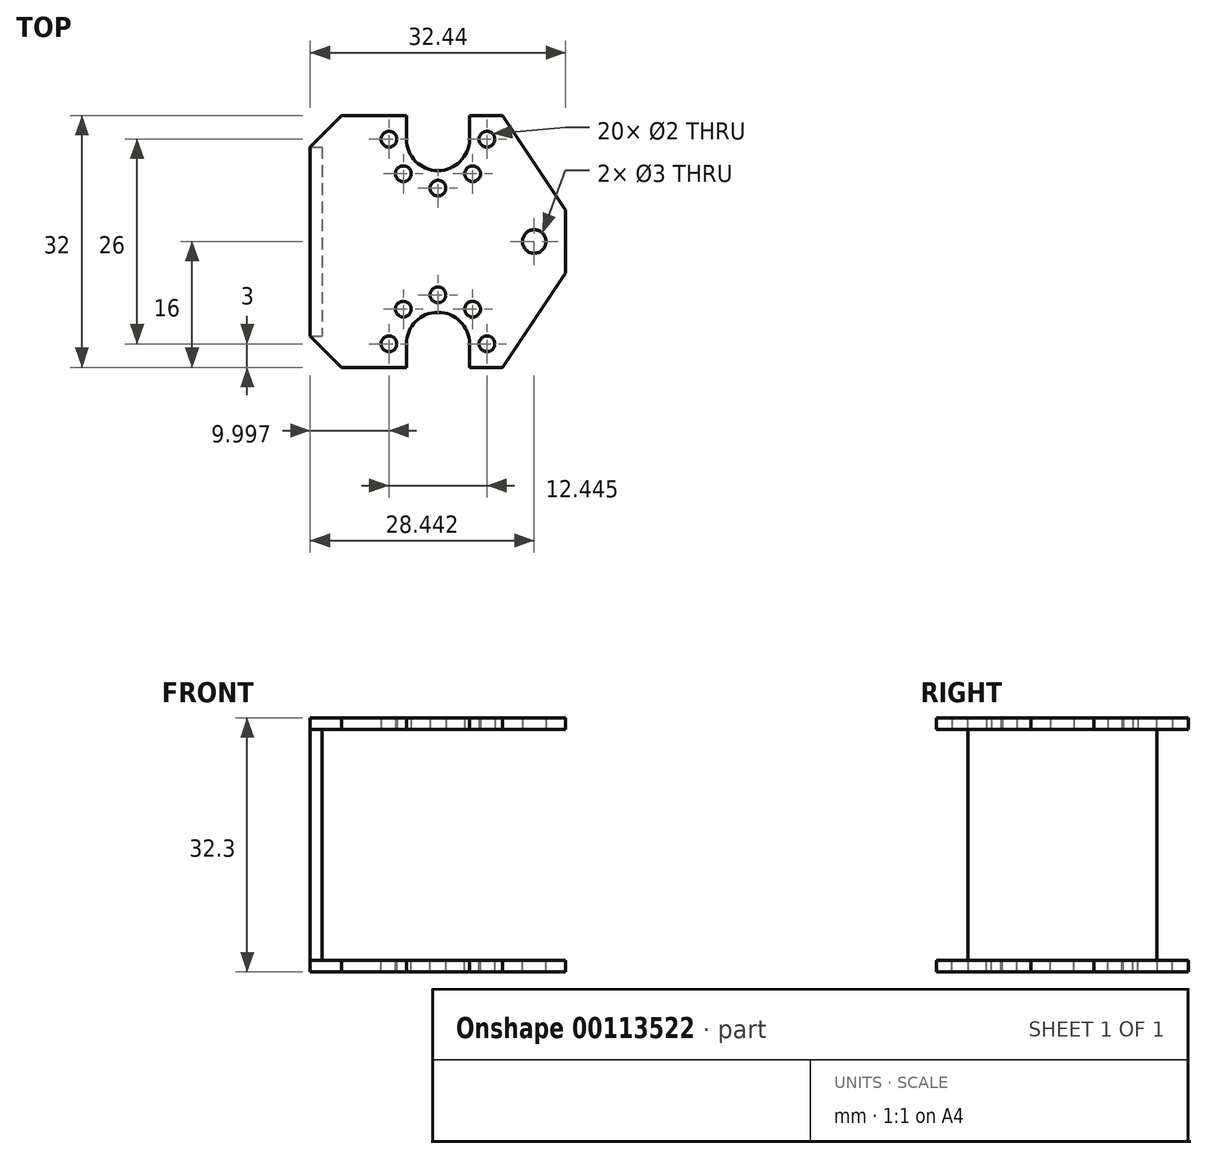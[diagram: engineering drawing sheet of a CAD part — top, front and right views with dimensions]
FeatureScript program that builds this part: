
annotation { "Feature Type Name" : "Feature", "Feature Type Description" : "" }
export const myFeature = defineFeature(function(context is Context, id is Id, definition is map)
    precondition{}
    {
        {
            var Q0;
            Q0=qCreatedBy(makeId("Top.planeOp"),FACE);
            var sketch = newSketch(context, id + "F0", { "sketchPlane" : qUnion([Q0])});
            skLineSegment(sketch, "E0.bottom", {"start": v(-16.22, 16) * mm, "end": v(-4, 16) * mm});
            skLineSegment(sketch, "E0.top", {"start": v(-16.22, -16) * mm, "end": v(-4, -16) * mm});
            skLineSegment(sketch, "E0.left", {"start": v(-16.22, 16) * mm, "end": v(-16.22, -16) * mm});
            skLineSegment(sketch, "E0.right", {"start": v(16.22, 16) * mm, "end": v(16.22, -16) * mm});
            skPoint(sketch, "E0.middle", {"position": v(0, 0) * mm});
            skArc(sketch, "E1", {"start": v(-4, 13) * mm, "mid": v(0, 9) * mm, "end": v(4, 13) * mm});
            skLineSegment(sketch, "E2.bottom", {"start": v(4.4, 8.6) * mm, "end": v(-4.4, 8.6) * mm, "construction": true});
            skLineSegment(sketch, "E2.top", {"start": v(4.4, 17.4) * mm, "end": v(-4.4, 17.4) * mm, "construction": true});
            skLineSegment(sketch, "E2.left", {"start": v(4.4, 8.6) * mm, "end": v(4.4, 17.4) * mm, "construction": true});
            skLineSegment(sketch, "E2.right", {"start": v(-4.4, 8.6) * mm, "end": v(-4.4, 17.4) * mm, "construction": true});
            skCircle(sketch, "E3", {"center": v(4.4, 8.6) * mm, "radius": 1 * mm});
            skCircle(sketch, "E4.1.0", {"center": v(6.22, 13) * mm, "radius": 1 * mm});
            skCircle(sketch, "E4.5.0", {"center": v(-6.22, 13) * mm, "radius": 1 * mm});
            skCircle(sketch, "E4.6.0", {"center": v(-4.4, 8.6) * mm, "radius": 1 * mm});
            skCircle(sketch, "E4.7.0", {"center": v(0, 6.78) * mm, "radius": 1 * mm});
            skLineSegment(sketch, "E5", {"start": v(-4, 13) * mm, "end": v(-4, 16) * mm});
            skLineSegment(sketch, "E6", {"start": v(4, 13) * mm, "end": v(4, 16) * mm});
            skLineSegment(sketch, "E7.trimOffspring", {"start": v(4, 16) * mm, "end": v(16.22, 16) * mm});
            skPoint(sketch, "E8.MirrorP", {"position": v(0, -13) * mm});
            skLineSegment(sketch, "E9.MirrorCS", {"start": v(-4, -13) * mm, "end": v(-4, -16) * mm});
            skCircle(sketch, "E10.MirrorC", {"center": v(0, -6.78) * mm, "radius": 1 * mm});
            skLineSegment(sketch, "E11.MirrorCS", {"start": v(4, -13) * mm, "end": v(4, -16) * mm});
            skCircle(sketch, "E12.MirrorC", {"center": v(-4.4, -8.6) * mm, "radius": 1 * mm});
            skCircle(sketch, "E13.MirrorC", {"center": v(6.22, -13) * mm, "radius": 1 * mm});
            skCircle(sketch, "E14.MirrorC", {"center": v(-6.22, -13) * mm, "radius": 1 * mm});
            skArc(sketch, "E15.MirrorCS", {"start": v(-4, -13) * mm, "mid": v(0, -9) * mm, "end": v(4, -13) * mm});
            skCircle(sketch, "E16.MirrorC", {"center": v(4.4, -8.6) * mm, "radius": 1 * mm});
            skLineSegment(sketch, "E17.trimOffspring", {"start": v(4, -16) * mm, "end": v(16.22, -16) * mm});
            skCircle(sketch, "E18", {"center": v(12.22, 0) * mm, "radius": 1.5 * mm});
            skSolve(sketch);
        }
        {
            var Q0;
            Q0=qSketchRegion(id+"F0",true);
            extrude(context, id + "F1", {"entities" : qUnion([Q0]), "depth" : 1.5 * mm});
        }
        {
            var Q0;
            Q0=makeQuery(id+"F1.opExtrude","CAP_FACE",FACE,{"disambiguationData":[OSD([sQuery(id+"F0.wireOp",EDGE,"E0.bottom"),sQuery(id+"F0.wireOp",EDGE,"E0.top"),sQuery(id+"F0.wireOp",EDGE,"E0.left"),sQuery(id+"F0.wireOp",EDGE,"E0.right"),sQuery(id+"F0.wireOp",EDGE,"E1"),sQuery(id+"F0.wireOp",EDGE,"E3"),sQuery(id+"F0.wireOp",EDGE,"E4.1.0"),sQuery(id+"F0.wireOp",EDGE,"E4.5.0"),sQuery(id+"F0.wireOp",EDGE,"E4.6.0"),sQuery(id+"F0.wireOp",EDGE,"E4.7.0"),sQuery(id+"F0.wireOp",EDGE,"E5"),sQuery(id+"F0.wireOp",EDGE,"E6"),sQuery(id+"F0.wireOp",EDGE,"E7.trimOffspring"),sQuery(id+"F0.wireOp",EDGE,"E9.MirrorCS"),sQuery(id+"F0.wireOp",EDGE,"E10.MirrorC"),sQuery(id+"F0.wireOp",EDGE,"E11.MirrorCS"),sQuery(id+"F0.wireOp",EDGE,"E12.MirrorC"),sQuery(id+"F0.wireOp",EDGE,"E13.MirrorC"),sQuery(id+"F0.wireOp",EDGE,"E14.MirrorC"),sQuery(id+"F0.wireOp",EDGE,"E15.MirrorCS"),sQuery(id+"F0.wireOp",EDGE,"E16.MirrorC"),sQuery(id+"F0.wireOp",EDGE,"E17.trimOffspring")])],"isStart":false});
            var sketch = newSketch(context, id + "F2", { "sketchPlane" : qUnion([Q0])});
            skPoint(sketch, "E19", {"position": v(6.22, 13) * mm});
            skPoint(sketch, "E20", {"position": v(6.22, -13) * mm});
            skLineSegment(sketch, "E21", {"start": v(8.22, 16) * mm, "end": v(16.22, 4) * mm});
            skLineSegment(sketch, "E22", {"start": v(16.22, 4) * mm, "end": v(16.22, 16) * mm});
            skLineSegment(sketch, "E23", {"start": v(16.22, 16) * mm, "end": v(8.22, 16) * mm});
            skLineSegment(sketch, "E24.MirrorCS", {"start": v(16.22, -16) * mm, "end": v(8.22, -16) * mm});
            skLineSegment(sketch, "E25.MirrorCS", {"start": v(16.22, -4) * mm, "end": v(16.22, -16) * mm});
            skLineSegment(sketch, "E26.MirrorCS", {"start": v(8.22, -16) * mm, "end": v(16.22, -4) * mm});
            skLineSegment(sketch, "E27", {"start": v(-16.22, 16) * mm, "end": v(-16.22, 12) * mm});
            skLineSegment(sketch, "E28", {"start": v(-16.22, 12) * mm, "end": v(-12.22, 16) * mm});
            skLineSegment(sketch, "E29", {"start": v(-12.22, 16) * mm, "end": v(-16.22, 16) * mm});
            skLineSegment(sketch, "E30.MirrorCS", {"start": v(-12.22, -16) * mm, "end": v(-16.22, -16) * mm});
            skLineSegment(sketch, "E31.MirrorCS", {"start": v(-16.22, -12) * mm, "end": v(-12.22, -16) * mm});
            skLineSegment(sketch, "E32.MirrorCS", {"start": v(-16.22, -16) * mm, "end": v(-16.22, -12) * mm});
            skSolve(sketch);
        }
        {
            var Q0;
            Q0=qSketchRegion(id+"F2",true);
            extrude(context, id + "F3", {"entities" : qUnion([Q0]), "operationType" : NewBodyOperationType.REMOVE, "endBound" : BoundingType.UP_TO_NEXT, "oppositeDirection" : true, "depth" : 25 * mm});
        }
        {
            var Q0;
            Q0=makeQuery(id+"F1.opExtrude","CAP_FACE",FACE,{"disambiguationData":[OSD([sQuery(id+"F0.wireOp",EDGE,"E0.bottom"),sQuery(id+"F0.wireOp",EDGE,"E0.top"),sQuery(id+"F0.wireOp",EDGE,"E0.left"),sQuery(id+"F0.wireOp",EDGE,"E0.right"),sQuery(id+"F0.wireOp",EDGE,"E1"),sQuery(id+"F0.wireOp",EDGE,"E3"),sQuery(id+"F0.wireOp",EDGE,"E4.1.0"),sQuery(id+"F0.wireOp",EDGE,"E4.5.0"),sQuery(id+"F0.wireOp",EDGE,"E4.6.0"),sQuery(id+"F0.wireOp",EDGE,"E4.7.0"),sQuery(id+"F0.wireOp",EDGE,"E5"),sQuery(id+"F0.wireOp",EDGE,"E6"),sQuery(id+"F0.wireOp",EDGE,"E7.trimOffspring"),sQuery(id+"F0.wireOp",EDGE,"E9.MirrorCS"),sQuery(id+"F0.wireOp",EDGE,"E10.MirrorC"),sQuery(id+"F0.wireOp",EDGE,"E11.MirrorCS"),sQuery(id+"F0.wireOp",EDGE,"E12.MirrorC"),sQuery(id+"F0.wireOp",EDGE,"E13.MirrorC"),sQuery(id+"F0.wireOp",EDGE,"E14.MirrorC"),sQuery(id+"F0.wireOp",EDGE,"E15.MirrorCS"),sQuery(id+"F0.wireOp",EDGE,"E16.MirrorC"),sQuery(id+"F0.wireOp",EDGE,"E17.trimOffspring")])],"isStart":true});
            var sketch = newSketch(context, id + "F4", { "sketchPlane" : qUnion([Q0])});
            skLineSegment(sketch, "E33.bottom", {"start": v(-16.22, -12) * mm, "end": v(-14.72, -12) * mm});
            skLineSegment(sketch, "E33.top", {"start": v(-16.22, 12) * mm, "end": v(-14.72, 12) * mm});
            skLineSegment(sketch, "E33.left", {"start": v(-16.22, -12) * mm, "end": v(-16.22, 12) * mm});
            skLineSegment(sketch, "E33.right", {"start": v(-14.72, -12) * mm, "end": v(-14.72, 12) * mm});
            skSolve(sketch);
        }
        {
            var Q0;
            Q0=qSketchRegion(id+"F4",true);
            extrude(context, id + "F5", {"entities" : qUnion([Q0]), "operationType" : NewBodyOperationType.ADD, "depth" : (29.3 / 2) * mm});
        }
        {
            var Q0;
            Q0=qCreatedBy(makeId("Top.planeOp"),FACE);
            cPlane(context, id + "F6", {"entities" : qUnion([Q0]), "cplaneType" : CPlaneType.OFFSET, "offset" : (29.3 / 2) * mm, "oppositeDirection" : true, "width" : 150 * mm, "height" : 150 * mm});
        }
        {
            var Q0;
            Q0=makeQuery(id+"F1.opExtrude","SWEPT_BODY",BODY,{"disambiguationData":[OSD([sQuery(id+"F0.wireOp",EDGE,"E0.bottom"),sQuery(id+"F0.wireOp",EDGE,"E0.top"),sQuery(id+"F0.wireOp",EDGE,"E0.left"),sQuery(id+"F0.wireOp",EDGE,"E0.right"),sQuery(id+"F0.wireOp",EDGE,"E1"),sQuery(id+"F0.wireOp",EDGE,"E3"),sQuery(id+"F0.wireOp",EDGE,"E4.1.0"),sQuery(id+"F0.wireOp",EDGE,"E4.5.0"),sQuery(id+"F0.wireOp",EDGE,"E4.6.0"),sQuery(id+"F0.wireOp",EDGE,"E4.7.0"),sQuery(id+"F0.wireOp",EDGE,"E5"),sQuery(id+"F0.wireOp",EDGE,"E6"),sQuery(id+"F0.wireOp",EDGE,"E7.trimOffspring"),sQuery(id+"F0.wireOp",EDGE,"E9.MirrorCS"),sQuery(id+"F0.wireOp",EDGE,"E10.MirrorC"),sQuery(id+"F0.wireOp",EDGE,"E11.MirrorCS"),sQuery(id+"F0.wireOp",EDGE,"E12.MirrorC"),sQuery(id+"F0.wireOp",EDGE,"E13.MirrorC"),sQuery(id+"F0.wireOp",EDGE,"E14.MirrorC"),sQuery(id+"F0.wireOp",EDGE,"E15.MirrorCS"),sQuery(id+"F0.wireOp",EDGE,"E16.MirrorC"),sQuery(id+"F0.wireOp",EDGE,"E17.trimOffspring")])]});
            var Q1;
            Q1=qCreatedBy(id+"F6.planeOp",FACE);
            mirror(context, id + "F7", {"operationType" : NewBodyOperationType.ADD, "entities" : qUnion([Q0]), "mirrorPlane" : qUnion([Q1])});
        }
    });
